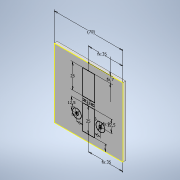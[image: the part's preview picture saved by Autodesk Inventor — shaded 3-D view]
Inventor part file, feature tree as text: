
AUTODESK INVENTOR PART (.ipt)
format: ipt  version: 2022.2 (Build 262287010, 287A)  size: 119,296 bytes
history: native  units: mm
features: sketch x2, extrude x1
ambient origin geometry x8: Origin, YZ Plane, XZ Plane, XY Plane, X Axis, Y Axis, Z Axis, Center Point
bodies: Solid1 (feature_tree)
feature tree (3):
  extrude  "Extrusion1"  Depth=70.0mm
  sketch  "Esboço3"  dims[d2=3.0mm d3=0.0mm d10=70.0mm d11=12.0mm d12=25.0mm d13=7.0mm d14=35.0mm d15=12.0mm d16=25.0mm d17=7.0mm d18=35.0mm d21=3.0mm d22=12.5mm d24=9.0mm d25=6.0mm d26=3.0mm d27=9.0mm d28=6.0mm d29=12.5mm]
  sketch  "Sketch1"  dims[d0=70.0mm d1=70.0mm]
